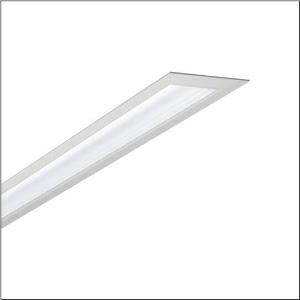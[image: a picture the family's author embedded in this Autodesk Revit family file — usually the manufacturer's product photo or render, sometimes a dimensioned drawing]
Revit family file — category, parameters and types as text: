
# Revit family: silica_r_5mx12wd1w4a_d237
name_source: partatom
category: Lighting Fixtures
units: mm (PartAtom-declared; Revit-internal decimal feet)

## family parameters
Cut with Voids When Loaded = No
Host = Face
Light Source = No
Part Type = Normal
Room Calculation Point = No
Round Connector Dimension = Use Diameter
Shared = No

## types (1)
- --- (1 x LED, 4680 lm, 29.3 W, 4000K)
    Apparent Load = 29 VA
    CIE Flux Codes = 70 95 99 100 100
    Color Rendering = 80
    Color Temperature = 4000K
    Default Elevation = 1800 mm
    Description = Silica®, office luminaire, primary light control with wallwasher, of aluminium, light emission: direct distribution, primary light characteristic: asymmetric, installation type: recessed, LED, rated luminous flux: 4.680lm, luminous efficacy: 160lm/W, light colour: 840, colour temperature: 4000K, control gear: ECG DALI, with terminal, 3+2-pole, max. 2.5mm², mains connection: 230V, AC, 50/60Hz, rated input power: 29W, luminaire housing, of aluminium, matt pure white (RAL 9010), length: 1.462mm, width: 93mm, height: 60mm, end cap, of diecast zinc, pure white (RAL 9010), protection rating (complete): IP20, insulation class (complete): insulation class I (protective earthing), certification: CE, permissible operating ambient temperature: 0..+35°C, standard: EN 50419, packaging unit: 1 piece
    Height = 0 mm  [stored 0 ft]
    Lamp = 1 x LED
    Lamp Light Flux = 4680 lm
    Lamp Power = 29.3 W
    Lamp count = 1
    Length = 1462 mm
    Luminous efficacy = 160 lm/W
    Manufacturer = Siteco
    ModVariant = No
    Model = 5MX12WD1W4A
    Mounting Place = Ceiling
    Mounting Type = Recessed
    Number of Poles = 1
    OnlyDefault = Yes
    Power Factor = 1
    Product Name = Silica®
    Product group = office luminaire | ceiling recessed
    ProductGroupID = 400
    Protection Class = Protection class I
    Protection Degree = IP 20
    RLX_Detail_Level = 1
    RLX_Emergency_Light_Flux = 0 lm
    RLX_Emergency_Type = 0
    RLX_Emergency_Type_DB = No
    RlxData = <blob elided: 24605 chars, md5=11cd0805>
    Socket = socket
    Standby Power = 0 W
    System Light Flux = 4680 lm
    System Power = 29 W
    Type Comments = factory setting: luminous flux: 100 % | dim-lin: 254 | 164 mA
    Type Image = l_1004825.jpg
    URL = http://relux.com
    VarID = @adj_172760
    Voltage = 0 V
    Weight = 0.00 kg
    Width = 93 mm

note: [stored X ft] marks values corroborated as IEEE doubles in the binary element streams (Revit-internal decimal feet)

## geometry (parser evidence)
native form markers: Blend x4, Sweep x10
no freeform markers — native parametric forms only
